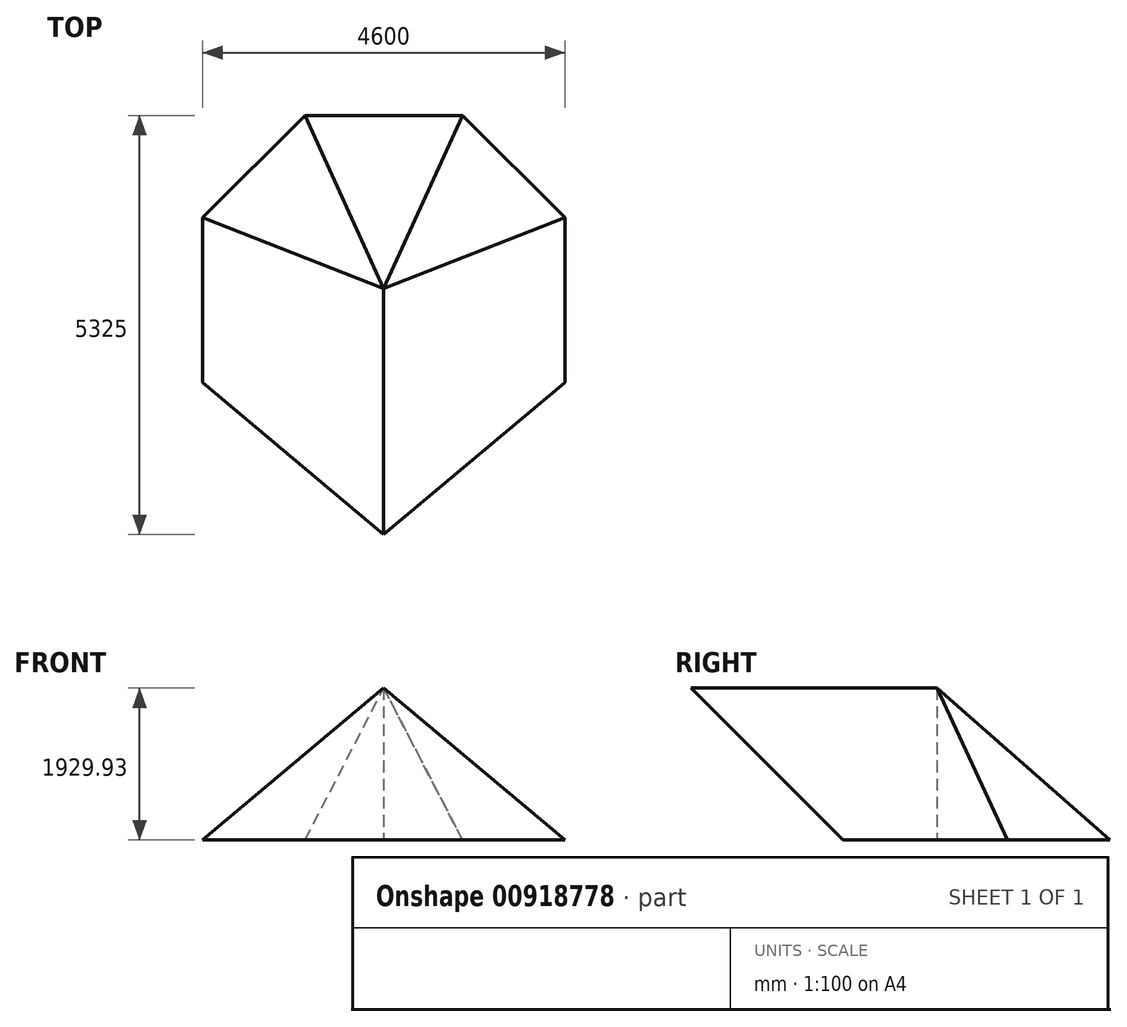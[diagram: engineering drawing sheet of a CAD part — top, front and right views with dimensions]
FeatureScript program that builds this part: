
annotation { "Feature Type Name" : "Feature", "Feature Type Description" : "" }
export const myFeature = defineFeature(function(context is Context, id is Id, definition is map)
    precondition{}
    {
        {
            var Q0;
            Q0=qCreatedBy(makeId("Top.planeOp"),FACE);
            var sketch = newSketch(context, id + "F0", { "sketchPlane" : qUnion([Q0])});
            skLineSegment(sketch, "E0.bottom", {"start": v(2300, -3250) * mm, "end": v(-2300, -3250) * mm, "construction": true});
            skLineSegment(sketch, "E0.top", {"start": v(2300, 3250) * mm, "end": v(-2300, 3250) * mm, "construction": true});
            skLineSegment(sketch, "E0.left", {"start": v(2300, -3250) * mm, "end": v(2300, 3250) * mm, "construction": true});
            skLineSegment(sketch, "E0.right", {"start": v(-2300, -3250) * mm, "end": v(-2300, 3250) * mm, "construction": true});
            skPoint(sketch, "E0.middle", {"position": v(0, 0) * mm});
            skLineSegment(sketch, "E1", {"start": v(0, 3250) * mm, "end": v(0, 0) * mm, "construction": true});
            skLineSegment(sketch, "E2", {"start": v(0, 0) * mm, "end": v(0, -3250) * mm, "construction": true});
            skLineSegment(sketch, "E3", {"start": v(-2300, 1950) * mm, "end": v(-1000, 3250) * mm, "construction": true});
            skLineSegment(sketch, "E4", {"start": v(-1000, 3250) * mm, "end": v(0, 3250) * mm, "construction": true});
            skLineSegment(sketch, "E5", {"start": v(0, 3250) * mm, "end": v(1000, 3250) * mm, "construction": true});
            skLineSegment(sketch, "E6", {"start": v(-2300, 1950) * mm, "end": v(0, 1050) * mm, "construction": true});
            skLineSegment(sketch, "E7", {"start": v(0, 1050) * mm, "end": v(-1000, 3250) * mm, "construction": true});
            skLineSegment(sketch, "E8", {"start": v(1000, 3250) * mm, "end": v(0, 1050) * mm, "construction": true});
            skLineSegment(sketch, "E9", {"start": v(2300, 1950) * mm, "end": v(0, 1050) * mm, "construction": true});
            skLineSegment(sketch, "E10", {"start": v(0, 1050) * mm, "end": v(-2300, 1050) * mm, "construction": true});
            skLineSegment(sketch, "E11", {"start": v(0, 1050) * mm, "end": v(2300, 1050) * mm, "construction": true});
            skLineSegment(sketch, "E12", {"start": v(1000, 3250) * mm, "end": v(2300, 1950) * mm, "construction": true});
            skLineSegment(sketch, "E13", {"start": v(-2300, -3250) * mm, "end": v(-2300, 1950) * mm});
            skLineSegment(sketch, "E14", {"start": v(-1000, 3250) * mm, "end": v(-2300, 1950) * mm});
            skLineSegment(sketch, "E15", {"start": v(-1000, 3250) * mm, "end": v(1000, 3250) * mm});
            skLineSegment(sketch, "E16", {"start": v(1000, 3250) * mm, "end": v(2300, 1950) * mm});
            skLineSegment(sketch, "E17", {"start": v(2300, 1950) * mm, "end": v(2300, -3250) * mm});
            skLineSegment(sketch, "E18", {"start": v(-2300, -3250) * mm, "end": v(2300, -3250) * mm});
            skLineSegment(sketch, "E19", {"start": v(-2300, 1950) * mm, "end": v(0, 1050) * mm});
            skLineSegment(sketch, "E20", {"start": v(0, 1050) * mm, "end": v(2300, 1950) * mm});
            skLineSegment(sketch, "E21", {"start": v(-1000, 3250) * mm, "end": v(0, 1050) * mm});
            skLineSegment(sketch, "E22", {"start": v(1000, 3250) * mm, "end": v(0, 1050) * mm});
            skSolve(sketch);
        }
        {
            var Q0;
            Q0=makeQuery(id+"F0.imprint","IMPRINT",FACE,{"disambiguationData":[TD([[makeQuery(id+"F0.imprint","IMPRINT",EDGE,{"derivedFrom":sQuery(id+"F0.wireOp",EDGE,"E13")}),-1.0]])]});
            extrude(context, id + "F1", {"entities" : qUnion([Q0]), "depth" : 3000 * mm, "offsetDistance" : 25 * mm});
        }
        {
            var Q0;
            Q0=makeQuery(id+"F1.opExtrude","SWEPT_FACE",FACE,{"disambiguationData":[OSD([sQuery(id+"F0.wireOp",EDGE,"E18")])]});
            var sketch = newSketch(context, id + "F2", { "sketchPlane" : qUnion([Q0])});
            skLineSegment(sketch, "E23", {"start": v(-2300, 0) * mm, "end": v(0, 1929.93) * mm});
            skLineSegment(sketch, "E24", {"start": v(0, 1929.93) * mm, "end": v(2300, 0) * mm});
            skSolve(sketch);
        }
        {
            var Q0;
            Q0=makeQuery(id+"F2.imprint","IMPRINT",FACE,{"disambiguationData":[TD([[makeQuery(id+"F2.imprint","IMPRINT",EDGE,{"derivedFrom":sQuery(id+"F2.wireOp",EDGE,"E23")}),1.0]])]});
            extrude(context, id + "F3", {"entities" : qUnion([Q0]), "operationType" : NewBodyOperationType.REMOVE, "endBound" : BoundingType.THROUGH_ALL, "oppositeDirection" : true, "depth" : 25 * mm, "offsetDistance" : 25 * mm});
        }
        {
            var Q0;
            Q0=makeQuery(id+"F0.imprint","IMPRINT",FACE,{"disambiguationData":[TD([[makeQuery(id+"F0.imprint","IMPRINT",EDGE,{"derivedFrom":sQuery(id+"F0.wireOp",EDGE,"E15")}),-1.0]])]});
            var Q1;
            Q1=makeQuery(id+"F3.boolean.opBoolean","INTERSECT",VERTEX,{"derivedFrom":[makeQuery(id+"F1.opExtrude","SWEPT_FACE",FACE,{"disambiguationData":[OSD([sQuery(id+"F0.wireOp",EDGE,"E19")])]}),makeQuery(id+"F1.opExtrude","SWEPT_FACE",FACE,{"disambiguationData":[OSD([sQuery(id+"F0.wireOp",EDGE,"E20")])]}),makeQuery(id+"F3.opExtrude","SWEPT_FACE",FACE,{"disambiguationData":[OSD([sQuery(id+"F2.wireOp",EDGE,"E23")])]}),makeQuery(id+"F3.opExtrude","SWEPT_FACE",FACE,{"disambiguationData":[OSD([sQuery(id+"F2.wireOp",EDGE,"E24")])]})]});
            extrude(context, id + "F4", {"entities" : qUnion([Q0]), "endBound" : BoundingType.UP_TO_VERTEX, "depth" : 25 * mm, "endBoundEntityVertex" : qUnion([Q1]), "offsetDistance" : 25 * mm});
        }
        {
            var Q0;
            Q0=makeQuery(id+"F4.opExtrude","CAP_EDGE",EDGE,{"disambiguationData":[OSD([sQuery(id+"F0.wireOp",EDGE,"E15")])],"isStart":false});
            chamfer(context, id + "F5", {"entities" : qUnion([Q0]), "chamferType" : ChamferType.OFFSET_ANGLE, "width" : 2200 * mm, "oppositeDirection" : true, "angle" : 41.25 * degree, "tangentPropagation" : true});
        }
        {
            var Q0;
            Q0=makeQuery(id+"F0.imprint","IMPRINT",FACE,{"disambiguationData":[TD([[makeQuery(id+"F0.imprint","IMPRINT",EDGE,{"derivedFrom":sQuery(id+"F0.wireOp",EDGE,"E14")}),1.0]])]});
            var Q1;
            Q1=makeQuery(id+"F3.boolean.opBoolean","INTERSECT",VERTEX,{"derivedFrom":[makeQuery(id+"F1.opExtrude","SWEPT_FACE",FACE,{"disambiguationData":[OSD([sQuery(id+"F0.wireOp",EDGE,"E19")])]}),makeQuery(id+"F1.opExtrude","SWEPT_FACE",FACE,{"disambiguationData":[OSD([sQuery(id+"F0.wireOp",EDGE,"E20")])]}),makeQuery(id+"F3.opExtrude","SWEPT_FACE",FACE,{"disambiguationData":[OSD([sQuery(id+"F2.wireOp",EDGE,"E23")])]}),makeQuery(id+"F3.opExtrude","SWEPT_FACE",FACE,{"disambiguationData":[OSD([sQuery(id+"F2.wireOp",EDGE,"E24")])]})]});
            extrude(context, id + "F6", {"entities" : qUnion([Q0]), "endBound" : BoundingType.UP_TO_VERTEX, "depth" : 25 * mm, "endBoundEntityVertex" : qUnion([Q1]), "offsetDistance" : 25 * mm});
        }
        {
            var Q0;
            Q0=makeQuery(id+"F6.opExtrude","CAP_EDGE",EDGE,{"disambiguationData":[OSD([sQuery(id+"F0.wireOp",EDGE,"E14")])],"isStart":false});
            chamfer(context, id + "F7", {"entities" : qUnion([Q0]), "chamferType" : ChamferType.OFFSET_ANGLE, "width" : 2262.5 * mm, "oppositeDirection" : false, "angle" : 40.45 * degree, "tangentPropagation" : true});
        }
        {
            var Q0;
            Q0=makeQuery(id+"F0.imprint","IMPRINT",FACE,{"disambiguationData":[TD([[makeQuery(id+"F0.imprint","IMPRINT",EDGE,{"derivedFrom":sQuery(id+"F0.wireOp",EDGE,"E16")}),-1.0]])]});
            var Q1;
            {var subQ0=sQuery(id+"F0.wireOp",EDGE,"E21");var subQ1=sQuery(id+"F0.wireOp",EDGE,"E14");Q1=makeQuery(id+"F7.opChamfer","BLEND_VERTEX",VERTEX,{"blendedFrom":[makeQuery(id+"F6.opExtrude","CAP_EDGE",EDGE,{"disambiguationData":[OSD([subQ1])],"isStart":false}),makeQuery(id+"F6.opExtrude","CAP_FACE",FACE,{"disambiguationData":[OSD([subQ1,sQuery(id+"F0.wireOp",EDGE,"E19"),subQ0])],"isStart":false}),makeQuery(id+"F6.opExtrude","SWEPT_FACE",FACE,{"disambiguationData":[OSD([subQ0])]})],"blendedInto":[makeQuery(id+"F6.opExtrude","CAP_FACE",FACE,{"disambiguationData":[OSD([subQ1,sQuery(id+"F0.wireOp",EDGE,"E19"),subQ0])],"isStart":false}),makeQuery(id+"F6.opExtrude","SWEPT_FACE",FACE,{"disambiguationData":[OSD([subQ0])]})]});}
            extrude(context, id + "F8", {"entities" : qUnion([Q0]), "endBound" : BoundingType.UP_TO_VERTEX, "depth" : 25 * mm, "endBoundEntityVertex" : qUnion([Q1]), "offsetDistance" : 25 * mm});
        }
        {
            var Q0;
            Q0=makeQuery(id+"F8.opExtrude","CAP_EDGE",EDGE,{"disambiguationData":[OSD([sQuery(id+"F0.wireOp",EDGE,"E16")])],"isStart":false});
            chamfer(context, id + "F9", {"entities" : qUnion([Q0]), "chamferType" : ChamferType.OFFSET_ANGLE, "width" : 2262.5 * mm, "oppositeDirection" : true, "angle" : 40.45 * degree, "tangentPropagation" : true});
        }
        {
            var Q0;
            Q0=qCreatedBy(makeId("Right.planeOp"),FACE);
            cPlane(context, id + "F10", {"entities" : qUnion([Q0]), "cplaneType" : CPlaneType.OFFSET, "offset" : 3000 * mm, "width" : 150 * mm, "height" : 150 * mm});
        }
        {
            var Q0;
            Q0=qCreatedBy(id+"F10.planeOp",FACE);
            var sketch = newSketch(context, id + "F11", { "sketchPlane" : qUnion([Q0])});
            skLineSegment(sketch, "E25", {"start": v(-2075, 1929.93) * mm, "end": v(-145.07, 0) * mm});
            skLineSegment(sketch, "E26", {"start": v(-145.07, 0) * mm, "end": v(-3250, 0) * mm});
            skLineSegment(sketch, "E27", {"start": v(-3250, 0) * mm, "end": v(-3250, 1929.93) * mm});
            skLineSegment(sketch, "E28", {"start": v(-3250, 1929.93) * mm, "end": v(-2075, 1929.93) * mm});
            skSolve(sketch);
        }
        {
            var Q0;
            Q0=makeQuery(id+"F11.imprint","IMPRINT",FACE,{"disambiguationData":[TD([[makeQuery(id+"F11.imprint","IMPRINT",EDGE,{"derivedFrom":sQuery(id+"F11.wireOp",EDGE,"E25")}),-1.0]])]});
            extrude(context, id + "F12", {"entities" : qUnion([Q0]), "operationType" : NewBodyOperationType.REMOVE, "endBound" : BoundingType.THROUGH_ALL, "oppositeDirection" : true, "depth" : 25 * mm, "offsetDistance" : 25 * mm});
        }
    });
